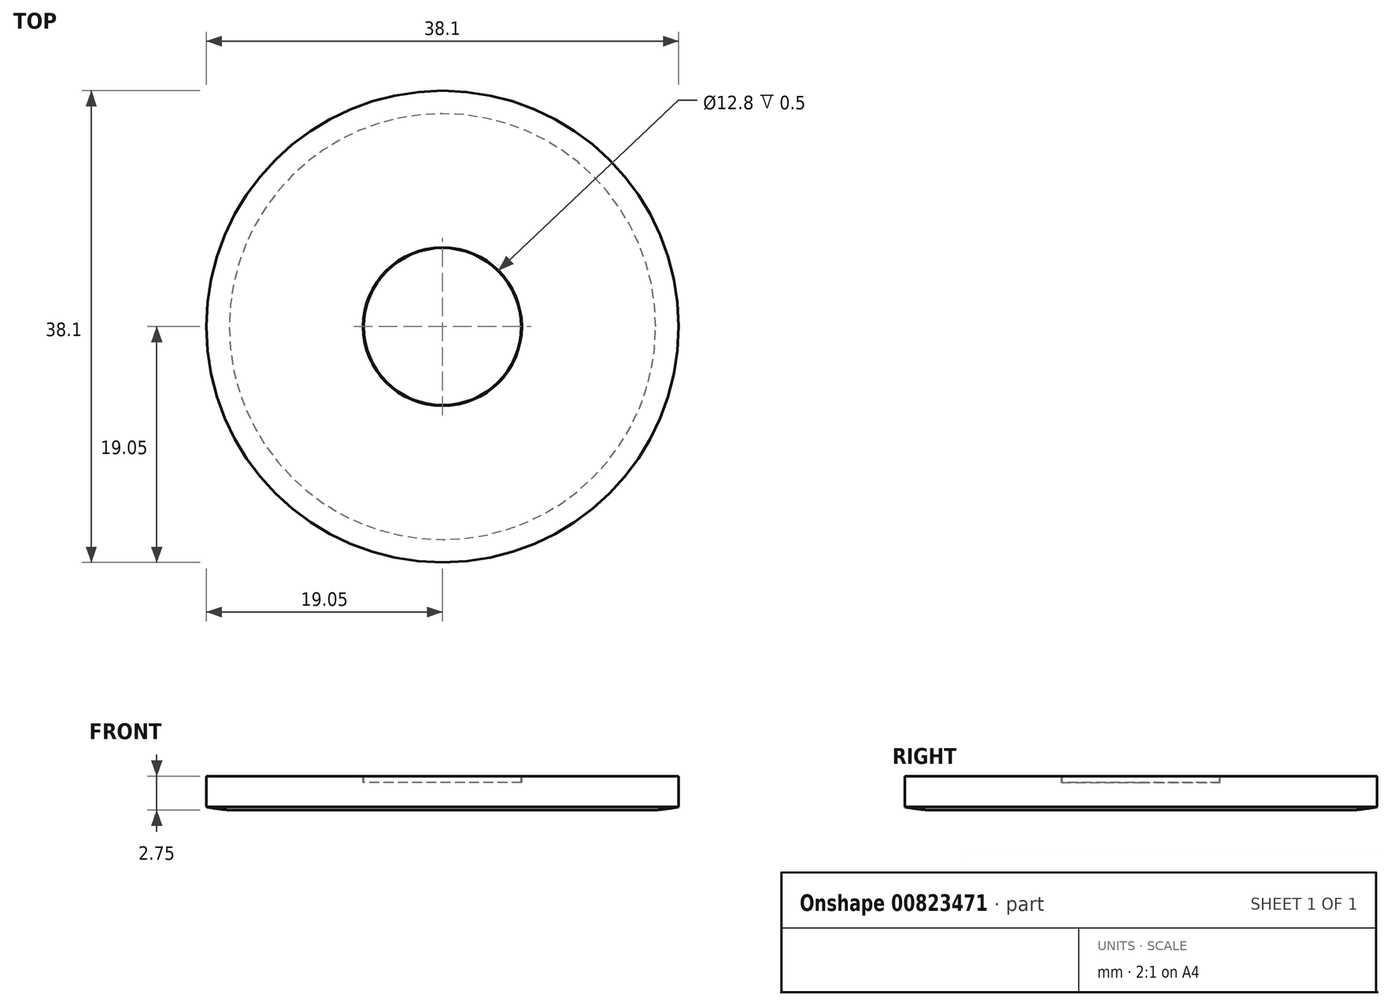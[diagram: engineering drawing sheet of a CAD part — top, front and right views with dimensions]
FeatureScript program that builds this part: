
annotation { "Feature Type Name" : "Feature", "Feature Type Description" : "" }
export const myFeature = defineFeature(function(context is Context, id is Id, definition is map)
    precondition{}
    {
        {
            var Q0;
            Q0=qCreatedBy(makeId("Top.planeOp"),FACE);
            var sketch = newSketch(context, id + "F0", { "sketchPlane" : qUnion([Q0])});
            skCircle(sketch, "E0", {"center": v(0, 0) * mm, "radius": 19.05 * mm});
            skSolve(sketch);
        }
        {
            var Q0;
            Q0=makeQuery(id+"F0.imprint","IMPRINT",FACE,{"disambiguationData":[TD([[makeQuery(id+"F0.imprint","IMPRINT",EDGE,{"derivedFrom":sQuery(id+"F0.wireOp",EDGE,"E0")}),1.0]])]});
            extrude(context, id + "F1", {"entities" : qUnion([Q0]), "depth" : 2.5 * mm, "offsetDistance" : 25 * mm});
        }
        {
            var Q0;
            Q0=makeQuery(id+"F1.opExtrude","CAP_FACE",FACE,{"disambiguationData":[OSD([sQuery(id+"F0.wireOp",EDGE,"E0")])],"isStart":false});
            var sketch = newSketch(context, id + "F2", { "sketchPlane" : qUnion([Q0])});
            skCircle(sketch, "E1", {"center": v(0, 0) * mm, "radius": 6.35 * mm});
            skCircle(sketch, "E2", {"center": v(0, 0) * mm, "radius": 6.4 * mm});
            skSolve(sketch);
        }
        {
            var Q0;
            Q0=makeQuery(id+"F2.imprint","IMPRINT",FACE,{"disambiguationData":[TD([[makeQuery(id+"F2.imprint","IMPRINT",EDGE,{"derivedFrom":sQuery(id+"F2.wireOp",EDGE,"E1")}),-1.0]])]});
            extrude(context, id + "F3", {"entities" : qUnion([Q0]), "operationType" : NewBodyOperationType.REMOVE, "oppositeDirection" : true, "depth" : .5 * mm, "offsetDistance" : 25 * mm});
        }
        {
            var Q0;
            Q0=qCreatedBy(makeId("Front.planeOp"),FACE);
            var sketch = newSketch(context, id + "F4", { "sketchPlane" : qUnion([Q0])});
            skLineSegment(sketch, "E3.0", {"start": v(-19.05, 0) * mm, "end": v(0, 0) * mm});
            skArc(sketch, "E4", {"start": v(-19.05, 0) * mm, "mid": v(-18.12, -0.14) * mm, "end": v(-17.2, -0.25) * mm});
            skLineSegment(sketch, "E5", {"start": v(0, -0.25) * mm, "end": v(-17.2, -0.25) * mm});
            skLineSegment(sketch, "E6", {"start": v(-17.2, -0.25) * mm, "end": v(0, -0.25) * mm});
            skLineSegment(sketch, "E7", {"start": v(0, 0) * mm, "end": v(0, -0.25) * mm});
            skPoint(sketch, "E8.orphan", {"position": v(19.05, 0) * mm});
            skSolve(sketch);
        }
        {
            var Q0;
            Q0=makeQuery(id+"F4.imprint","IMPRINT",FACE,{"disambiguationData":[TD([[makeQuery(id+"F4.imprint","IMPRINT",EDGE,{"derivedFrom":sQuery(id+"F4.wireOp",EDGE,"E3.0")}),-1.0]])]});
            var Q1;
            Q1=sQuery(id+"F4.wireOp",EDGE,"E7");
            revolve(context, id + "F5", {"surfaceOperationType" : NewSurfaceOperationType.NEW, "entities" : qUnion([Q0]), "axis" : qUnion([Q1]), "revolveType" : RevolveType.FULL});
        }
    });
